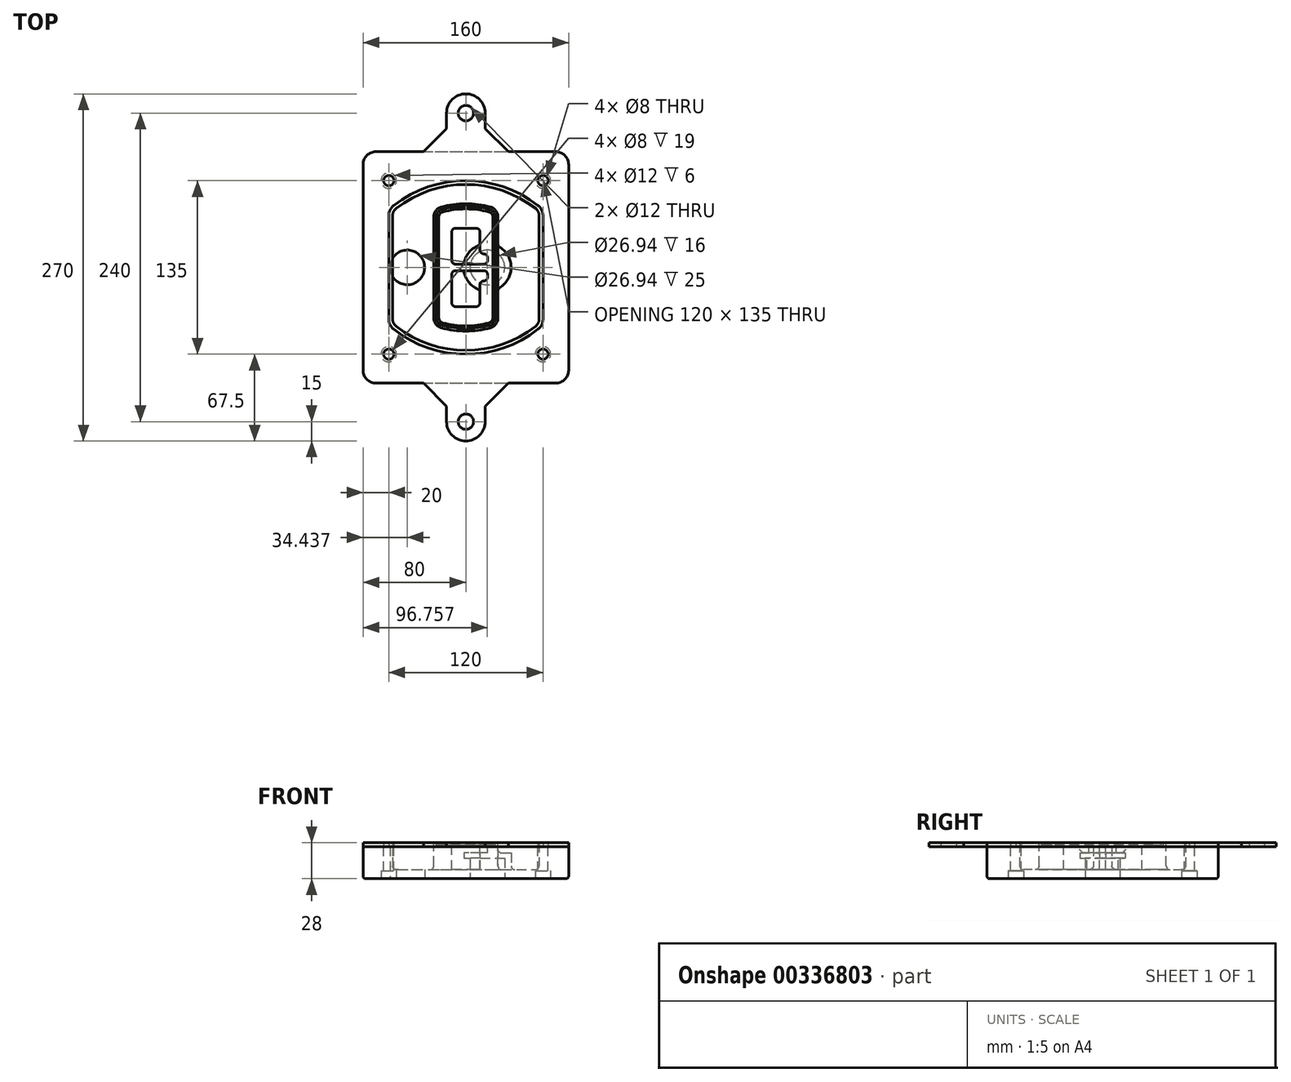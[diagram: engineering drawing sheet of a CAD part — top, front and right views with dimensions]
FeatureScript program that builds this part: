
annotation { "Feature Type Name" : "Feature", "Feature Type Description" : "" }
export const myFeature = defineFeature(function(context is Context, id is Id, definition is map)
    precondition{}
    {
        {
            var Q0;
            Q0=qCreatedBy(makeId("Top.planeOp"),FACE);
            var sketch = newSketch(context, id + "F0", { "sketchPlane" : qUnion([Q0])});
            skPoint(sketch, "E0.rect.middle", {"position": v(0, 0) * mm});
            skLineSegment(sketch, "E1.bottom", {"start": v(-70, -90) * mm, "end": v(70, -90) * mm});
            skLineSegment(sketch, "E1.top", {"start": v(-70, 90) * mm, "end": v(70, 90) * mm});
            skLineSegment(sketch, "E1.left", {"start": v(-80, -80) * mm, "end": v(-80, 80) * mm});
            skLineSegment(sketch, "E1.right", {"start": v(80, -80) * mm, "end": v(80, 80) * mm});
            skLineSegment(sketch, "E2", {"start": v(-80, 90) * mm, "end": v(80, -90) * mm, "construction": true});
            skLineSegment(sketch, "E3", {"start": v(80, 90) * mm, "end": v(-80, -90) * mm, "construction": true});
            skCircle(sketch, "E4", {"center": v(-60, 67.5) * mm, "radius": 4 * mm});
            skCircle(sketch, "E5", {"center": v(60, 67.5) * mm, "radius": 4 * mm});
            skCircle(sketch, "E6", {"center": v(60, -67.5) * mm, "radius": 4 * mm});
            skCircle(sketch, "E7", {"center": v(-60, -67.5) * mm, "radius": 4 * mm});
            skLineSegment(sketch, "E8", {"start": v(-60, 67.5) * mm, "end": v(60, 67.5) * mm, "construction": true});
            skLineSegment(sketch, "E9", {"start": v(60, 67.5) * mm, "end": v(60, -67.5) * mm, "construction": true});
            skLineSegment(sketch, "E10", {"start": v(60, -67.5) * mm, "end": v(-60, -67.5) * mm, "construction": true});
            skLineSegment(sketch, "E11", {"start": v(-60, -67.5) * mm, "end": v(-60, 67.5) * mm, "construction": true});
            skLineSegment(sketch, "E12", {"start": v(-60, 40.3) * mm, "end": v(-60, -40.3) * mm});
            skLineSegment(sketch, "E13", {"start": v(60, 40.3) * mm, "end": v(60, -40.3) * mm});
            skArc(sketch, "E14", {"start": v(56.15, 48.18) * mm, "mid": v(0, 67.5) * mm, "end": v(-56.15, 48.18) * mm});
            skArc(sketch, "E15", {"start": v(-56.15, -48.18) * mm, "mid": v(0, -67.5) * mm, "end": v(56.15, -48.18) * mm});
            skLineSegment(sketch, "E16", {"start": v(-60, 0) * mm, "end": v(60, 0) * mm, "construction": true});
            skPoint(sketch, "E17.visualSharp", {"position": v(-60, -45) * mm});
            skArc(sketch, "E17.filletArc", {"start": v(-60, -40.3) * mm, "mid": v(-58.99, -44.68) * mm, "end": v(-56.15, -48.18) * mm});
            skPoint(sketch, "E18.visualSharp", {"position": v(-60, 45) * mm});
            skArc(sketch, "E18.filletArc", {"start": v(-56.15, 48.18) * mm, "mid": v(-58.99, 44.68) * mm, "end": v(-60, 40.3) * mm});
            skPoint(sketch, "E19.visualSharp", {"position": v(60, 45) * mm});
            skArc(sketch, "E19.filletArc", {"start": v(60, 40.3) * mm, "mid": v(58.99, 44.68) * mm, "end": v(56.15, 48.18) * mm});
            skPoint(sketch, "E20.visualSharp", {"position": v(60, -45) * mm});
            skArc(sketch, "E20.filletArc", {"start": v(56.15, -48.18) * mm, "mid": v(58.99, -44.68) * mm, "end": v(60, -40.3) * mm});
            skPoint(sketch, "E21.visualSharp", {"position": v(-80, 90) * mm});
            skArc(sketch, "E21.filletArc", {"start": v(-70, 90) * mm, "mid": v(-77.07, 87.07) * mm, "end": v(-80, 80) * mm});
            skPoint(sketch, "E22.visualSharp", {"position": v(80, 90) * mm});
            skArc(sketch, "E22.filletArc", {"start": v(80, 80) * mm, "mid": v(77.07, 87.07) * mm, "end": v(70, 90) * mm});
            skPoint(sketch, "E23.visualSharp", {"position": v(80, -90) * mm});
            skArc(sketch, "E23.filletArc", {"start": v(70, -90) * mm, "mid": v(77.07, -87.07) * mm, "end": v(80, -80) * mm});
            skPoint(sketch, "E24.visualSharp", {"position": v(-80, -90) * mm});
            skArc(sketch, "E24.filletArc", {"start": v(-80, -80) * mm, "mid": v(-77.07, -87.07) * mm, "end": v(-70, -90) * mm});
            skArc(sketch, "E25.0", {"start": v(57, 40.3) * mm, "mid": v(56.3, 43.36) * mm, "end": v(54.3, 45.81) * mm});
            skLineSegment(sketch, "E25.1", {"start": v(57, 40.3) * mm, "end": v(57, -40.3) * mm});
            skArc(sketch, "E25.2", {"start": v(54.3, -45.81) * mm, "mid": v(56.3, -43.36) * mm, "end": v(57, -40.3) * mm});
            skArc(sketch, "E25.3", {"start": v(-54.3, -45.81) * mm, "mid": v(0, -64.5) * mm, "end": v(54.3, -45.81) * mm});
            skArc(sketch, "E25.4", {"start": v(-57, -40.3) * mm, "mid": v(-56.3, -43.36) * mm, "end": v(-54.3, -45.81) * mm});
            skArc(sketch, "E25.5", {"start": v(54.3, 45.81) * mm, "mid": v(0, 64.5) * mm, "end": v(-54.3, 45.81) * mm});
            skLineSegment(sketch, "E25.6", {"start": v(-57, 40.3) * mm, "end": v(-57, -40.3) * mm});
            skArc(sketch, "E25.7", {"start": v(-54.3, 45.81) * mm, "mid": v(-56.3, 43.36) * mm, "end": v(-57, 40.3) * mm});
            skArc(sketch, "E26.0", {"start": v(-58.62, 51.33) * mm, "mid": v(-62.58, 46.43) * mm, "end": v(-64, 40.3) * mm});
            skArc(sketch, "E26.1", {"start": v(58.62, 51.33) * mm, "mid": v(0, 71.5) * mm, "end": v(-58.62, 51.33) * mm});
            skArc(sketch, "E26.2", {"start": v(64, 40.3) * mm, "mid": v(62.58, 46.43) * mm, "end": v(58.62, 51.33) * mm});
            skLineSegment(sketch, "E26.3", {"start": v(64, 40.3) * mm, "end": v(64, -40.3) * mm});
            skArc(sketch, "E26.4", {"start": v(58.62, -51.33) * mm, "mid": v(62.58, -46.43) * mm, "end": v(64, -40.3) * mm});
            skLineSegment(sketch, "E26.5", {"start": v(-64, 40.3) * mm, "end": v(-64, -40.3) * mm});
            skArc(sketch, "E26.6", {"start": v(-58.62, -51.33) * mm, "mid": v(0, -71.5) * mm, "end": v(58.62, -51.33) * mm});
            skArc(sketch, "E26.7", {"start": v(-64, -40.3) * mm, "mid": v(-62.58, -46.43) * mm, "end": v(-58.62, -51.33) * mm});
            skSolve(sketch);
        }
        {
            var Q0;
            Q0=makeQuery(id+"F0.imprint","IMPRINT",FACE,{"disambiguationData":[TD([[makeQuery(id+"F0.imprint","IMPRINT",EDGE,{"derivedFrom":sQuery(id+"F0.wireOp",EDGE,"E1.bottom")}),1.0]])]});
            var Q1;
            Q1=makeQuery(id+"F0.imprint","IMPRINT",FACE,{"disambiguationData":[TD([[makeQuery(id+"F0.imprint","IMPRINT",EDGE,{"derivedFrom":sQuery(id+"F0.wireOp",EDGE,"E12")}),1.0]])]});
            var Q2;
            Q2=makeQuery(id+"F0.imprint","IMPRINT",FACE,{"disambiguationData":[TD([[makeQuery(id+"F0.imprint","IMPRINT",EDGE,{"derivedFrom":sQuery(id+"F0.wireOp",EDGE,"E25.0")}),1.0]])]});
            var Q3;
            Q3=makeQuery(id+"F0.imprint","IMPRINT",FACE,{"disambiguationData":[TD([[makeQuery(id+"F0.imprint","IMPRINT",EDGE,{"derivedFrom":sQuery(id+"F0.wireOp",EDGE,"E12")}),-1.0]])]});
            extrude(context, id + "F1", {"entities" : qUnion([Q0, Q1, Q2, Q3]), "oppositeDirection" : true, "depth" : 25 * mm});
        }
        {
            var Q0;
            Q0=makeQuery(id+"F0.imprint","IMPRINT",FACE,{"disambiguationData":[TD([[makeQuery(id+"F0.imprint","IMPRINT",EDGE,{"derivedFrom":sQuery(id+"F0.wireOp",EDGE,"E12")}),1.0]])]});
            extrude(context, id + "F2", {"entities" : qUnion([Q0]), "operationType" : NewBodyOperationType.ADD, "depth" : 3 * mm});
        }
        {
            var Q0;
            Q0=makeQuery(id+"F0.imprint","IMPRINT",FACE,{"disambiguationData":[TD([[makeQuery(id+"F0.imprint","IMPRINT",EDGE,{"derivedFrom":sQuery(id+"F0.wireOp",EDGE,"E25.0")}),1.0]])]});
            extrude(context, id + "F3", {"entities" : qUnion([Q0]), "operationType" : NewBodyOperationType.REMOVE, "oppositeDirection" : true, "depth" : 18 * mm});
        }
        {
            var Q0;
            Q0=makeQuery(id+"F2.opExtrude","CAP_FACE",FACE,{"disambiguationData":[OSD([sQuery(id+"F0.wireOp",EDGE,"E12"),sQuery(id+"F0.wireOp",EDGE,"E13"),sQuery(id+"F0.wireOp",EDGE,"E14"),sQuery(id+"F0.wireOp",EDGE,"E15"),sQuery(id+"F0.wireOp",EDGE,"E17.filletArc"),sQuery(id+"F0.wireOp",EDGE,"E18.filletArc"),sQuery(id+"F0.wireOp",EDGE,"E19.filletArc"),sQuery(id+"F0.wireOp",EDGE,"E20.filletArc"),sQuery(id+"F0.wireOp",EDGE,"E25.0"),sQuery(id+"F0.wireOp",EDGE,"E25.1"),sQuery(id+"F0.wireOp",EDGE,"E25.2"),sQuery(id+"F0.wireOp",EDGE,"E25.3"),sQuery(id+"F0.wireOp",EDGE,"E25.4"),sQuery(id+"F0.wireOp",EDGE,"E25.5"),sQuery(id+"F0.wireOp",EDGE,"E25.6"),sQuery(id+"F0.wireOp",EDGE,"E25.7")])],"isStart":false});
            var sketch = newSketch(context, id + "F4", { "sketchPlane" : qUnion([Q0])});
            skArc(sketch, "E27.0", {"start": v(-19.08, -46.97) * mm, "mid": v(0, -49.5) * mm, "end": v(19.08, -46.97) * mm});
            skArc(sketch, "E28.0", {"start": v(19.08, 46.97) * mm, "mid": v(0, 49.5) * mm, "end": v(-19.08, 46.97) * mm});
            skLineSegment(sketch, "E29", {"start": v(-25, 39.25) * mm, "end": v(-25, -39.25) * mm});
            skLineSegment(sketch, "E30", {"start": v(25, 39.25) * mm, "end": v(25, -39.25) * mm});
            skLineSegment(sketch, "E31", {"start": v(-25, 45.1) * mm, "end": v(25, 45.1) * mm, "construction": true});
            skLineSegment(sketch, "E32", {"start": v(-25, -45.1) * mm, "end": v(25, -45.1) * mm, "construction": true});
            skPoint(sketch, "E33.visualSharp", {"position": v(-25, 45.1) * mm});
            skArc(sketch, "E33.filletArc", {"start": v(-19.08, 46.97) * mm, "mid": v(-23.35, 44.11) * mm, "end": v(-25, 39.25) * mm});
            skPoint(sketch, "E34.visualSharp", {"position": v(25, 45.1) * mm});
            skArc(sketch, "E34.filletArc", {"start": v(25, 39.25) * mm, "mid": v(23.35, 44.11) * mm, "end": v(19.08, 46.97) * mm});
            skPoint(sketch, "E35.visualSharp", {"position": v(25, -45.1) * mm});
            skArc(sketch, "E35.filletArc", {"start": v(19.08, -46.97) * mm, "mid": v(23.35, -44.11) * mm, "end": v(25, -39.25) * mm});
            skPoint(sketch, "E36.visualSharp", {"position": v(-25, -45.1) * mm});
            skArc(sketch, "E36.filletArc", {"start": v(-25, -39.25) * mm, "mid": v(-23.35, -44.11) * mm, "end": v(-19.08, -46.97) * mm});
            skArc(sketch, "E37.0", {"start": v(54.3, 45.81) * mm, "mid": v(0, 64.5) * mm, "end": v(-54.3, 45.81) * mm});
            skArc(sketch, "E37.1", {"start": v(-54.3, 45.81) * mm, "mid": v(-56.3, 43.36) * mm, "end": v(-57, 40.3) * mm});
            skLineSegment(sketch, "E37.2", {"start": v(-57, 40.3) * mm, "end": v(-57, -40.3) * mm});
            skArc(sketch, "E37.3", {"start": v(-57, -40.3) * mm, "mid": v(-56.3, -43.36) * mm, "end": v(-54.3, -45.81) * mm});
            skArc(sketch, "E37.4", {"start": v(-54.3, -45.81) * mm, "mid": v(0, -64.5) * mm, "end": v(54.3, -45.81) * mm});
            skArc(sketch, "E37.5", {"start": v(54.3, -45.81) * mm, "mid": v(56.3, -43.36) * mm, "end": v(57, -40.3) * mm});
            skLineSegment(sketch, "E37.6", {"start": v(57, 40.3) * mm, "end": v(57, -40.3) * mm});
            skArc(sketch, "E37.7", {"start": v(57, 40.3) * mm, "mid": v(56.3, 43.36) * mm, "end": v(54.3, 45.81) * mm});
            skLineSegment(sketch, "E38.0", {"start": v(23, 39.25) * mm, "end": v(23, -39.25) * mm});
            skArc(sketch, "E38.1", {"start": v(18.56, -45.04) * mm, "mid": v(21.76, -42.9) * mm, "end": v(23, -39.25) * mm});
            skArc(sketch, "E38.2", {"start": v(-18.56, -45.04) * mm, "mid": v(0, -47.5) * mm, "end": v(18.56, -45.04) * mm});
            skArc(sketch, "E38.3", {"start": v(-23, -39.25) * mm, "mid": v(-21.76, -42.9) * mm, "end": v(-18.56, -45.04) * mm});
            skLineSegment(sketch, "E38.4", {"start": v(-23, 39.25) * mm, "end": v(-23, -39.25) * mm});
            skArc(sketch, "E38.5", {"start": v(23, 39.25) * mm, "mid": v(21.76, 42.9) * mm, "end": v(18.56, 45.04) * mm});
            skArc(sketch, "E38.6", {"start": v(-18.56, 45.04) * mm, "mid": v(-21.76, 42.9) * mm, "end": v(-23, 39.25) * mm});
            skArc(sketch, "E38.7", {"start": v(18.56, 45.04) * mm, "mid": v(0, 47.5) * mm, "end": v(-18.56, 45.04) * mm});
            skArc(sketch, "E39.0", {"start": v(21, 39.25) * mm, "mid": v(20.18, 41.68) * mm, "end": v(18.04, 43.1) * mm});
            skLineSegment(sketch, "E39.1", {"start": v(21, 39.25) * mm, "end": v(21, -39.25) * mm});
            skArc(sketch, "E39.2", {"start": v(18.04, -43.1) * mm, "mid": v(20.18, -41.68) * mm, "end": v(21, -39.25) * mm});
            skArc(sketch, "E39.3", {"start": v(-18.04, -43.1) * mm, "mid": v(0, -45.5) * mm, "end": v(18.04, -43.1) * mm});
            skArc(sketch, "E39.4", {"start": v(-21, -39.25) * mm, "mid": v(-20.18, -41.68) * mm, "end": v(-18.04, -43.1) * mm});
            skArc(sketch, "E39.5", {"start": v(18.04, 43.1) * mm, "mid": v(0, 45.5) * mm, "end": v(-18.04, 43.1) * mm});
            skLineSegment(sketch, "E39.6", {"start": v(-21, 39.25) * mm, "end": v(-21, -39.25) * mm});
            skArc(sketch, "E39.7", {"start": v(-18.04, 43.1) * mm, "mid": v(-20.18, 41.68) * mm, "end": v(-21, 39.25) * mm});
            skLineSegment(sketch, "E40", {"start": v(-25, 0) * mm, "end": v(25, 0) * mm, "construction": true});
            skLineSegment(sketch, "E41", {"start": v(-11, 5.5) * mm, "end": v(-11, 27.5) * mm});
            skLineSegment(sketch, "E42", {"start": v(-8, 30.5) * mm, "end": v(8, 30.5) * mm});
            skLineSegment(sketch, "E43", {"start": v(11, 27.5) * mm, "end": v(11, 13.5) * mm});
            skLineSegment(sketch, "E44", {"start": v(14, 10.5) * mm, "end": v(14, 10.5) * mm});
            skLineSegment(sketch, "E45", {"start": v(17, 7.5) * mm, "end": v(17, 5.5) * mm});
            skLineSegment(sketch, "E46", {"start": v(14, 2.5) * mm, "end": v(-8, 2.5) * mm});
            skPoint(sketch, "E47.visualSharp", {"position": v(-11, 30.5) * mm});
            skArc(sketch, "E47.filletArc", {"start": v(-8, 30.5) * mm, "mid": v(-10.12, 29.62) * mm, "end": v(-11, 27.5) * mm});
            skPoint(sketch, "E48.visualSharp", {"position": v(11, 30.5) * mm});
            skArc(sketch, "E48.filletArc", {"start": v(11, 27.5) * mm, "mid": v(10.12, 29.62) * mm, "end": v(8, 30.5) * mm});
            skPoint(sketch, "E49.visualSharp", {"position": v(11, 10.5) * mm});
            skArc(sketch, "E49.filletArc", {"start": v(11, 13.5) * mm, "mid": v(11.88, 11.38) * mm, "end": v(14, 10.5) * mm});
            skPoint(sketch, "E50.visualSharp", {"position": v(17, 10.5) * mm});
            skArc(sketch, "E50.filletArc", {"start": v(17, 7.5) * mm, "mid": v(16.12, 9.62) * mm, "end": v(14, 10.5) * mm});
            skPoint(sketch, "E51.visualSharp", {"position": v(17, 2.5) * mm});
            skArc(sketch, "E51.filletArc", {"start": v(14, 2.5) * mm, "mid": v(16.12, 3.38) * mm, "end": v(17, 5.5) * mm});
            skPoint(sketch, "E52.visualSharp", {"position": v(-11, 2.5) * mm});
            skArc(sketch, "E52.filletArc", {"start": v(-11, 5.5) * mm, "mid": v(-10.12, 3.38) * mm, "end": v(-8, 2.5) * mm});
            skLineSegment(sketch, "E53.0.MirrorCS", {"start": v(14, -2.5) * mm, "end": v(-8, -2.5) * mm});
            skArc(sketch, "E54.0.MirrorCS", {"start": v(-11, -5.5) * mm, "mid": v(-10.12, -3.38) * mm, "end": v(-8, -2.5) * mm});
            skLineSegment(sketch, "E55.0.MirrorCS", {"start": v(-11, -5.5) * mm, "end": v(-11, -27.5) * mm});
            skArc(sketch, "E56.0.MirrorCS", {"start": v(-8, -30.5) * mm, "mid": v(-10.12, -29.62) * mm, "end": v(-11, -27.5) * mm});
            skLineSegment(sketch, "E57.0.MirrorCS", {"start": v(-8, -30.5) * mm, "end": v(8, -30.5) * mm});
            skArc(sketch, "E58.0.MirrorCS", {"start": v(11, -27.5) * mm, "mid": v(10.12, -29.62) * mm, "end": v(8, -30.5) * mm});
            skLineSegment(sketch, "E59.0.MirrorCS", {"start": v(11, -27.5) * mm, "end": v(11, -13.5) * mm});
            skArc(sketch, "E60.0.MirrorCS", {"start": v(11, -13.5) * mm, "mid": v(11.88, -11.38) * mm, "end": v(14, -10.5) * mm});
            skArc(sketch, "E61.0.MirrorCS", {"start": v(17, -7.5) * mm, "mid": v(16.12, -9.62) * mm, "end": v(14, -10.5) * mm});
            skLineSegment(sketch, "E62.0.MirrorCS", {"start": v(17, -7.5) * mm, "end": v(17, -5.5) * mm});
            skArc(sketch, "E63.0.MirrorCS", {"start": v(14, -2.5) * mm, "mid": v(16.12, -3.38) * mm, "end": v(17, -5.5) * mm});
            skSolve(sketch);
        }
        {
            var Q0;
            Q0=makeQuery(id+"F4.imprint","IMPRINT",FACE,{"disambiguationData":[TD([[makeQuery(id+"F4.imprint","IMPRINT",EDGE,{"derivedFrom":sQuery(id+"F4.wireOp",EDGE,"E27.0")}),1.0]])]});
            var Q1;
            Q1=makeQuery(id+"F4.imprint","IMPRINT",FACE,{"disambiguationData":[TD([[makeQuery(id+"F4.imprint","IMPRINT",EDGE,{"derivedFrom":sQuery(id+"F4.wireOp",EDGE,"E38.0")}),-1.0]])]});
            var Q2;
            Q2=makeQuery(id+"F4.imprint","IMPRINT",FACE,{"disambiguationData":[TD([[makeQuery(id+"F4.imprint","IMPRINT",EDGE,{"derivedFrom":sQuery(id+"F4.wireOp",EDGE,"E39.0")}),1.0]])]});
            extrude(context, id + "F5", {"entities" : qUnion([Q0, Q1, Q2]), "operationType" : NewBodyOperationType.ADD, "endBound" : BoundingType.UP_TO_NEXT, "oppositeDirection" : true, "depth" : 25 * mm});
        }
        {
            var Q0;
            Q0=makeQuery(id+"F4.imprint","IMPRINT",FACE,{"disambiguationData":[TD([[makeQuery(id+"F4.imprint","IMPRINT",EDGE,{"derivedFrom":sQuery(id+"F4.wireOp",EDGE,"E38.0")}),-1.0]])]});
            extrude(context, id + "F6", {"entities" : qUnion([Q0]), "operationType" : NewBodyOperationType.REMOVE, "oppositeDirection" : true, "depth" : 2 * mm});
        }
        {
            var Q0;
            Q0=makeQuery(id+"F1.opExtrude","CAP_FACE",FACE,{"disambiguationData":[OSD([sQuery(id+"F0.wireOp",EDGE,"E1.bottom"),sQuery(id+"F0.wireOp",EDGE,"E1.top"),sQuery(id+"F0.wireOp",EDGE,"E1.left"),sQuery(id+"F0.wireOp",EDGE,"E1.right"),sQuery(id+"F0.wireOp",EDGE,"E4"),sQuery(id+"F0.wireOp",EDGE,"E5"),sQuery(id+"F0.wireOp",EDGE,"E6"),sQuery(id+"F0.wireOp",EDGE,"E7"),sQuery(id+"F0.wireOp",EDGE,"E21.filletArc"),sQuery(id+"F0.wireOp",EDGE,"E22.filletArc"),sQuery(id+"F0.wireOp",EDGE,"E23.filletArc"),sQuery(id+"F0.wireOp",EDGE,"E24.filletArc")])],"isStart":false});
            var sketch = newSketch(context, id + "F7", { "sketchPlane" : qUnion([Q0])});
            skCircle(sketch, "E64", {"center": v(16.76, 0) * mm, "radius": 13.47 * mm});
            skCircle(sketch, "E65", {"center": v(-45.56, 0) * mm, "radius": 13.47 * mm});
            skLineSegment(sketch, "E66", {"start": v(80, 0) * mm, "end": v(-80, 0) * mm});
            skCircle(sketch, "E67", {"center": v(16.76, 0) * mm, "radius": 18.47 * mm});
            skCircle(sketch, "E68", {"center": v(60, -67.5) * mm, "radius": 6 * mm});
            skCircle(sketch, "E69", {"center": v(-60, -67.5) * mm, "radius": 6 * mm});
            skCircle(sketch, "E70", {"center": v(-60, 67.5) * mm, "radius": 6 * mm});
            skCircle(sketch, "E71", {"center": v(60, 67.5) * mm, "radius": 6 * mm});
            skSolve(sketch);
        }
        {
            var Q0;
            {var subQ1=sQuery(id+"F7.wireOp",EDGE,"E66");var subQ4=sQuery(id+"F7.wireOp",EDGE,"E64");var subQ6=makeQuery(id+"F7.imprint","INTERSECT",VERTEX,{"disambiguationData":[OD(0.0)],"derivedFrom":[subQ4,subQ1]});Q0=makeQuery(id+"F7.imprint","IMPRINT",FACE,{"disambiguationData":[TD([[makeQuery(id+"F7.imprint","IMPRINT",EDGE,{"disambiguationData":[TD([[subQ6,-1.0]])],"derivedFrom":subQ4}),-1.0]])]});}
            var Q1;
            {var subQ0=sQuery(id+"F7.wireOp",EDGE,"E66");var subQ1=sQuery(id+"F7.wireOp",EDGE,"E64");var subQ3=makeQuery(id+"F7.imprint","INTERSECT",VERTEX,{"disambiguationData":[OD(0.0)],"derivedFrom":[subQ1,subQ0]});Q1=makeQuery(id+"F7.imprint","IMPRINT",FACE,{"disambiguationData":[TD([[makeQuery(id+"F7.imprint","IMPRINT",EDGE,{"disambiguationData":[TD([[subQ3,-1.0]])],"derivedFrom":subQ1}),1.0]])]});}
            var Q2;
            {var subQ0=sQuery(id+"F7.wireOp",EDGE,"E66");var subQ1=sQuery(id+"F7.wireOp",EDGE,"E64");var subQ3=makeQuery(id+"F7.imprint","INTERSECT",VERTEX,{"disambiguationData":[OD(0.0)],"derivedFrom":[subQ1,subQ0]});Q2=makeQuery(id+"F7.imprint","IMPRINT",FACE,{"disambiguationData":[TD([[makeQuery(id+"F7.imprint","IMPRINT",EDGE,{"disambiguationData":[TD([[subQ3,1.0]])],"derivedFrom":subQ1}),1.0]])]});}
            var Q3;
            {var subQ1=sQuery(id+"F7.wireOp",EDGE,"E66");var subQ4=sQuery(id+"F7.wireOp",EDGE,"E64");var subQ6=makeQuery(id+"F7.imprint","INTERSECT",VERTEX,{"disambiguationData":[OD(0.0)],"derivedFrom":[subQ4,subQ1]});Q3=makeQuery(id+"F7.imprint","IMPRINT",FACE,{"disambiguationData":[TD([[makeQuery(id+"F7.imprint","IMPRINT",EDGE,{"disambiguationData":[TD([[subQ6,1.0]])],"derivedFrom":subQ4}),-1.0]])]});}
            extrude(context, id + "F8", {"entities" : qUnion([Q0, Q1, Q2, Q3]), "operationType" : NewBodyOperationType.ADD, "oppositeDirection" : true, "depth" : 20 * mm});
        }
        {
            var Q0;
            {var subQ0=sQuery(id+"F7.wireOp",EDGE,"E66");var subQ1=sQuery(id+"F7.wireOp",EDGE,"E64");var subQ3=makeQuery(id+"F7.imprint","INTERSECT",VERTEX,{"disambiguationData":[OD(0.0)],"derivedFrom":[subQ1,subQ0]});Q0=makeQuery(id+"F7.imprint","IMPRINT",FACE,{"disambiguationData":[TD([[makeQuery(id+"F7.imprint","IMPRINT",EDGE,{"disambiguationData":[TD([[subQ3,-1.0]])],"derivedFrom":subQ1}),1.0]])]});}
            var Q1;
            {var subQ0=sQuery(id+"F7.wireOp",EDGE,"E66");var subQ1=sQuery(id+"F7.wireOp",EDGE,"E64");var subQ3=makeQuery(id+"F7.imprint","INTERSECT",VERTEX,{"disambiguationData":[OD(0.0)],"derivedFrom":[subQ1,subQ0]});Q1=makeQuery(id+"F7.imprint","IMPRINT",FACE,{"disambiguationData":[TD([[makeQuery(id+"F7.imprint","IMPRINT",EDGE,{"disambiguationData":[TD([[subQ3,1.0]])],"derivedFrom":subQ1}),1.0]])]});}
            extrude(context, id + "F9", {"entities" : qUnion([Q0, Q1]), "operationType" : NewBodyOperationType.REMOVE, "oppositeDirection" : true, "depth" : 16 * mm});
        }
        {
            var Q0;
            {var subQ0=sQuery(id+"F7.wireOp",EDGE,"E66");var subQ1=sQuery(id+"F7.wireOp",EDGE,"E65");var subQ3=makeQuery(id+"F7.imprint","INTERSECT",VERTEX,{"disambiguationData":[OD(0.0)],"derivedFrom":[subQ1,subQ0]});Q0=makeQuery(id+"F7.imprint","IMPRINT",FACE,{"disambiguationData":[TD([[makeQuery(id+"F7.imprint","IMPRINT",EDGE,{"disambiguationData":[TD([[subQ3,-1.0]])],"derivedFrom":subQ1}),1.0]])]});}
            var Q1;
            {var subQ0=sQuery(id+"F7.wireOp",EDGE,"E66");var subQ1=sQuery(id+"F7.wireOp",EDGE,"E65");var subQ3=makeQuery(id+"F7.imprint","INTERSECT",VERTEX,{"disambiguationData":[OD(0.0)],"derivedFrom":[subQ1,subQ0]});Q1=makeQuery(id+"F7.imprint","IMPRINT",FACE,{"disambiguationData":[TD([[makeQuery(id+"F7.imprint","IMPRINT",EDGE,{"disambiguationData":[TD([[subQ3,1.0]])],"derivedFrom":subQ1}),1.0]])]});}
            extrude(context, id + "F10", {"entities" : qUnion([Q0, Q1]), "operationType" : NewBodyOperationType.REMOVE, "oppositeDirection" : true, "depth" : 25 * mm});
        }
        {
            var Q0;
            Q0=makeQuery(id+"F7.imprint","IMPRINT",FACE,{"disambiguationData":[TD([[makeQuery(id+"F7.imprint","IMPRINT",EDGE,{"derivedFrom":sQuery(id+"F7.wireOp",EDGE,"E68")}),1.0]])]});
            var Q1;
            Q1=makeQuery(id+"F7.imprint","IMPRINT",FACE,{"disambiguationData":[TD([[makeQuery(id+"F7.imprint","IMPRINT",EDGE,{"derivedFrom":makeQuery(id+"F1.opExtrude","CAP_EDGE",EDGE,{"disambiguationData":[OSD([sQuery(id+"F0.wireOp",EDGE,"E5")])],"isStart":false})}),-1.0]])]});
            var Q2;
            Q2=makeQuery(id+"F7.imprint","IMPRINT",FACE,{"disambiguationData":[TD([[makeQuery(id+"F7.imprint","IMPRINT",EDGE,{"derivedFrom":sQuery(id+"F7.wireOp",EDGE,"E69")}),1.0]])]});
            var Q3;
            Q3=makeQuery(id+"F7.imprint","IMPRINT",FACE,{"disambiguationData":[TD([[makeQuery(id+"F7.imprint","IMPRINT",EDGE,{"derivedFrom":makeQuery(id+"F1.opExtrude","CAP_EDGE",EDGE,{"disambiguationData":[OSD([sQuery(id+"F0.wireOp",EDGE,"E4")])],"isStart":false})}),-1.0]])]});
            var Q4;
            Q4=makeQuery(id+"F7.imprint","IMPRINT",FACE,{"disambiguationData":[TD([[makeQuery(id+"F7.imprint","IMPRINT",EDGE,{"derivedFrom":sQuery(id+"F7.wireOp",EDGE,"E70")}),1.0]])]});
            var Q5;
            Q5=makeQuery(id+"F7.imprint","IMPRINT",FACE,{"disambiguationData":[TD([[makeQuery(id+"F7.imprint","IMPRINT",EDGE,{"derivedFrom":makeQuery(id+"F1.opExtrude","CAP_EDGE",EDGE,{"disambiguationData":[OSD([sQuery(id+"F0.wireOp",EDGE,"E7")])],"isStart":false})}),-1.0]])]});
            var Q6;
            Q6=makeQuery(id+"F7.imprint","IMPRINT",FACE,{"disambiguationData":[TD([[makeQuery(id+"F7.imprint","IMPRINT",EDGE,{"derivedFrom":sQuery(id+"F7.wireOp",EDGE,"E71")}),1.0]])]});
            var Q7;
            Q7=makeQuery(id+"F7.imprint","IMPRINT",FACE,{"disambiguationData":[TD([[makeQuery(id+"F7.imprint","IMPRINT",EDGE,{"derivedFrom":makeQuery(id+"F1.opExtrude","CAP_EDGE",EDGE,{"disambiguationData":[OSD([sQuery(id+"F0.wireOp",EDGE,"E6")])],"isStart":false})}),-1.0]])]});
            extrude(context, id + "F11", {"entities" : qUnion([Q0, Q1, Q2, Q3, Q4, Q5, Q6, Q7]), "operationType" : NewBodyOperationType.REMOVE, "oppositeDirection" : true, "depth" : 6 * mm});
        }
        {
            var Q0;
            Q0=makeQuery(id+"F9.boolean.opBoolean","COPY",FACE,{"derivedFrom":makeQuery(id+"F9.opExtrude","CAP_FACE",FACE,{"disambiguationData":[OSD([sQuery(id+"F7.wireOp",EDGE,"E64")])],"isStart":false})});
            var sketch = newSketch(context, id + "F12", { "sketchPlane" : qUnion([Q0])});
            skArc(sketch, "E72.0", {"start": v(11, 17.55) * mm, "mid": v(2.57, 11.82) * mm, "end": v(-1.54, 2.5) * mm});
            skArc(sketch, "E72.1", {"start": v(-1.54, -2.5) * mm, "mid": v(2.57, -11.82) * mm, "end": v(11, -17.55) * mm});
            skLineSegment(sketch, "E73", {"start": v(-1.54, -2.5) * mm, "end": v(14, -2.5) * mm});
            skLineSegment(sketch, "E74.0", {"start": v(14, 2.5) * mm, "end": v(-1.54, 2.5) * mm});
            skArc(sketch, "E74.1", {"start": v(14, 2.5) * mm, "mid": v(16.12, 3.38) * mm, "end": v(17, 5.5) * mm});
            skLineSegment(sketch, "E74.2", {"start": v(17, 7.5) * mm, "end": v(17, 5.5) * mm});
            skArc(sketch, "E74.3", {"start": v(17, 7.5) * mm, "mid": v(16.12, 9.62) * mm, "end": v(14, 10.5) * mm});
            skArc(sketch, "E74.4", {"start": v(11, 13.5) * mm, "mid": v(11.88, 11.38) * mm, "end": v(14, 10.5) * mm});
            skLineSegment(sketch, "E74.5", {"start": v(11, 17.55) * mm, "end": v(11, 13.5) * mm});
            skLineSegment(sketch, "E74.7", {"start": v(14, -2.5) * mm, "end": v(-1.54, -2.5) * mm});
            skArc(sketch, "E74.8", {"start": v(14, -2.5) * mm, "mid": v(16.12, -3.38) * mm, "end": v(17, -5.5) * mm});
            skLineSegment(sketch, "E74.9", {"start": v(17, -7.5) * mm, "end": v(17, -5.5) * mm});
            skArc(sketch, "E74.10", {"start": v(17, -7.5) * mm, "mid": v(16.12, -9.62) * mm, "end": v(14, -10.5) * mm});
            skArc(sketch, "E74.11", {"start": v(11, -13.5) * mm, "mid": v(11.88, -11.38) * mm, "end": v(14, -10.5) * mm});
            skLineSegment(sketch, "E74.12", {"start": v(11, -17.55) * mm, "end": v(11, -13.5) * mm});
            skPoint(sketch, "E75.orphan", {"position": v(11, -27.5) * mm});
            skPoint(sketch, "E76.orphan", {"position": v(-8, -2.5) * mm});
            skPoint(sketch, "E77.orphan", {"position": v(-8, 2.5) * mm});
            skPoint(sketch, "E78.orphan", {"position": v(11, 27.5) * mm});
            skSolve(sketch);
        }
        {
            var Q0;
            {var subQ7=sQuery(id+"F12.wireOp",EDGE,"E72.0");var subQ14=sQuery(id+"F12.wireOp",EDGE,"E72.1");var subQ16=sQuery(id+"F12.wireOp",EDGE,"E74.1");var subQ18=sQuery(id+"F12.wireOp",EDGE,"E74.8");Q0=qUnion([makeQuery(id+"F12.imprint","IMPRINT",FACE,{"disambiguationData":[TD([[makeQuery(id+"F12.imprint","IMPRINT",EDGE,{"derivedFrom":subQ7}),1.0]])]}),makeQuery(id+"F12.imprint","IMPRINT",FACE,{"disambiguationData":[TD([[makeQuery(id+"F12.imprint","IMPRINT",EDGE,{"derivedFrom":subQ14}),1.0]])]}),makeQuery(id+"F12.imprint","IMPRINT",FACE,{"disambiguationData":[TD([[makeQuery(id+"F12.imprint","IMPRINT",EDGE,{"derivedFrom":subQ16}),1.0]])]}),makeQuery(id+"F12.imprint","IMPRINT",FACE,{"disambiguationData":[TD([[makeQuery(id+"F12.imprint","IMPRINT",EDGE,{"derivedFrom":subQ18}),-1.0]])]})]);}
            var Q1;
            Q1=makeQuery(id+"F5.boolean.opBoolean","SPLIT",FACE,{"disambiguationData":[TD([makeQuery(id+"F5.opExtrude","SWEPT_FACE",FACE,{"disambiguationData":[OSD([sQuery(id+"F4.wireOp",EDGE,"E41")])]})])],"derivedFrom":makeQuery(id+"F3.boolean.opBoolean","COPY",FACE,{"derivedFrom":makeQuery(id+"F3.opExtrude","CAP_FACE",FACE,{"disambiguationData":[OSD([sQuery(id+"F0.wireOp",EDGE,"E25.0"),sQuery(id+"F0.wireOp",EDGE,"E25.1"),sQuery(id+"F0.wireOp",EDGE,"E25.2"),sQuery(id+"F0.wireOp",EDGE,"E25.3"),sQuery(id+"F0.wireOp",EDGE,"E25.4"),sQuery(id+"F0.wireOp",EDGE,"E25.5"),sQuery(id+"F0.wireOp",EDGE,"E25.6"),sQuery(id+"F0.wireOp",EDGE,"E25.7")])],"isStart":false})})});
            extrude(context, id + "F13", {"entities" : qUnion([Q0]), "operationType" : NewBodyOperationType.REMOVE, "endBound" : BoundingType.UP_TO_SURFACE, "endBoundEntityFace" : qUnion([Q1]), "depth" : 25 * mm});
        }
        {
            var Q0;
            Q0=makeQuery(id+"F3.boolean.opBoolean","COPY",EDGE,{"derivedFrom":makeQuery(id+"F3.opExtrude","CAP_EDGE",EDGE,{"disambiguationData":[OSD([sQuery(id+"F0.wireOp",EDGE,"E25.6")])],"isStart":false})});
            var Q1;
            Q1=makeQuery(id+"F8.boolean.opBoolean","INTERSECT",EDGE,{"derivedFrom":[makeQuery(id+"F5.opExtrude","SWEPT_FACE",FACE,{"disambiguationData":[OSD([sQuery(id+"F4.wireOp",EDGE,"E30")])]}),makeQuery(id+"F8.opExtrude","CAP_FACE",FACE,{"disambiguationData":[OSD([sQuery(id+"F7.wireOp",EDGE,"E67")])],"isStart":false})]});
            var Q2;
            Q2=makeQuery(id+"F8.boolean.opBoolean","INTERSECT",EDGE,{"disambiguationData":[OD(1.0)],"derivedFrom":[makeQuery(id+"F5.opExtrude","SWEPT_FACE",FACE,{"disambiguationData":[OSD([sQuery(id+"F4.wireOp",EDGE,"E30")])]}),makeQuery(id+"F8.opExtrude","SWEPT_FACE",FACE,{"disambiguationData":[OSD([sQuery(id+"F7.wireOp",EDGE,"E67")])]})]});
            var Q3;
            {var subQ0=sQuery(id+"F4.wireOp",EDGE,"E30");Q3=makeQuery(id+"F8.boolean.opBoolean","SPLIT",EDGE,{"disambiguationData":[TD([makeQuery(id+"F5.opExtrude","SWEPT_FACE",FACE,{"disambiguationData":[OSD([sQuery(id+"F4.wireOp",EDGE,"E35.filletArc")])]})])],"derivedFrom":makeQuery(id+"F5.opExtrude","CAP_EDGE",EDGE,{"disambiguationData":[OSD([subQ0])],"isStart":false})});}
            var Q4;
            {var subQ0=sQuery(id+"F0.wireOp",EDGE,"E25.7");var subQ1=sQuery(id+"F0.wireOp",EDGE,"E25.1");var subQ2=sQuery(id+"F0.wireOp",EDGE,"E25.6");var subQ3=sQuery(id+"F0.wireOp",EDGE,"E25.5");var subQ4=sQuery(id+"F0.wireOp",EDGE,"E25.4");var subQ5=sQuery(id+"F0.wireOp",EDGE,"E25.0");var subQ6=sQuery(id+"F0.wireOp",EDGE,"E25.2");var subQ7=sQuery(id+"F0.wireOp",EDGE,"E25.3");Q4=makeQuery(id+"F8.boolean.opBoolean","INTERSECT",EDGE,{"derivedFrom":[makeQuery(id+"F5.boolean.opBoolean","SPLIT",FACE,{"disambiguationData":[TD([makeQuery(id+"F2.opExtrude","SWEPT_FACE",FACE,{"disambiguationData":[OSD([subQ5])]})])],"derivedFrom":makeQuery(id+"F3.boolean.opBoolean","COPY",FACE,{"derivedFrom":makeQuery(id+"F3.opExtrude","CAP_FACE",FACE,{"disambiguationData":[OSD([subQ5,subQ1,subQ6,subQ7,subQ4,subQ3,subQ2,subQ0])],"isStart":false})})}),makeQuery(id+"F8.opExtrude","SWEPT_FACE",FACE,{"disambiguationData":[OSD([sQuery(id+"F7.wireOp",EDGE,"E67")])]})]});}
            var Q5;
            Q5=makeQuery(id+"F8.boolean.opBoolean","INTERSECT",EDGE,{"disambiguationData":[OD(0.0)],"derivedFrom":[makeQuery(id+"F5.opExtrude","SWEPT_FACE",FACE,{"disambiguationData":[OSD([sQuery(id+"F4.wireOp",EDGE,"E30")])]}),makeQuery(id+"F8.opExtrude","SWEPT_FACE",FACE,{"disambiguationData":[OSD([sQuery(id+"F7.wireOp",EDGE,"E67")])]})]});
            fillet(context, id + "F14", {"entities" : qUnion([Q0, Q1, Q2, Q3, Q4, Q5]), "radius" : 3 * mm, "tangentPropagation" : true, "allowEdgeOverflow" : false});
        }
        {
            var Q0;
            Q0=makeQuery(id+"F1.opExtrude","CAP_EDGE",EDGE,{"disambiguationData":[OSD([sQuery(id+"F0.wireOp",EDGE,"E1.bottom")])],"isStart":false});
            fillet(context, id + "F15", {"entities" : qUnion([Q0]), "radius" : 2 * mm, "tangentPropagation" : true, "allowEdgeOverflow" : false});
        }
        {
            var Q0;
            {var subQ0=sQuery(id+"F0.wireOp",EDGE,"E21.filletArc");var subQ1=sQuery(id+"F0.wireOp",EDGE,"E7");var subQ2=sQuery(id+"F0.wireOp",EDGE,"E6");var subQ3=sQuery(id+"F0.wireOp",EDGE,"E5");var subQ4=sQuery(id+"F0.wireOp",EDGE,"E4");var subQ5=sQuery(id+"F0.wireOp",EDGE,"E22.filletArc");var subQ6=sQuery(id+"F0.wireOp",EDGE,"E1.bottom");var subQ7=sQuery(id+"F0.wireOp",EDGE,"E1.right");var subQ8=sQuery(id+"F0.wireOp",EDGE,"E1.top");var subQ9=sQuery(id+"F0.wireOp",EDGE,"E1.left");var subQ10=sQuery(id+"F0.wireOp",EDGE,"E23.filletArc");var subQ11=sQuery(id+"F0.wireOp",EDGE,"E24.filletArc");Q0=makeQuery(id+"F2.boolean.opBoolean","SPLIT",FACE,{"disambiguationData":[TD([makeQuery(id+"F1.opExtrude","SWEPT_FACE",FACE,{"disambiguationData":[OSD([subQ6])]})])],"derivedFrom":makeQuery(id+"F1.opExtrude","CAP_FACE",FACE,{"disambiguationData":[OSD([subQ6,subQ8,subQ9,subQ7,subQ4,subQ3,subQ2,subQ1,subQ0,subQ5,subQ10,subQ11])],"isStart":true})});}
            var sketch = newSketch(context, id + "F16", { "sketchPlane" : qUnion([Q0])});
            skLineSegment(sketch, "E79.0", {"start": v(-70, 90) * mm, "end": v(70, 90) * mm});
            skArc(sketch, "E79.1", {"start": v(-70, 90) * mm, "mid": v(-77.07, 87.07) * mm, "end": v(-80, 80) * mm});
            skLineSegment(sketch, "E79.2", {"start": v(-80, -80) * mm, "end": v(-80, 80) * mm});
            skCircle(sketch, "E79.3", {"center": v(-60, 67.5) * mm, "radius": 4 * mm});
            skArc(sketch, "E79.4", {"start": v(-56.15, 48.18) * mm, "mid": v(-58.99, 44.68) * mm, "end": v(-60, 40.3) * mm});
            skArc(sketch, "E79.5", {"start": v(56.15, 48.18) * mm, "mid": v(0, 67.5) * mm, "end": v(-56.15, 48.18) * mm});
            skLineSegment(sketch, "E79.6", {"start": v(-60, 40.3) * mm, "end": v(-60, -40.3) * mm});
            skArc(sketch, "E79.7", {"start": v(60, 40.3) * mm, "mid": v(58.99, 44.68) * mm, "end": v(56.15, 48.18) * mm});
            skLineSegment(sketch, "E79.8", {"start": v(60, 40.3) * mm, "end": v(60, -40.3) * mm});
            skLineSegment(sketch, "E79.9", {"start": v(80, -80) * mm, "end": v(80, 80) * mm});
            skArc(sketch, "E79.10", {"start": v(80, 80) * mm, "mid": v(77.07, 87.07) * mm, "end": v(70, 90) * mm});
            skCircle(sketch, "E79.11", {"center": v(60, 67.5) * mm, "radius": 4 * mm});
            skCircle(sketch, "E79.12", {"center": v(60, -67.5) * mm, "radius": 4 * mm});
            skArc(sketch, "E79.13", {"start": v(70, -90) * mm, "mid": v(77.07, -87.07) * mm, "end": v(80, -80) * mm});
            skArc(sketch, "E79.14", {"start": v(56.15, -48.18) * mm, "mid": v(58.99, -44.68) * mm, "end": v(60, -40.3) * mm});
            skArc(sketch, "E79.15", {"start": v(-56.15, -48.18) * mm, "mid": v(0, -67.5) * mm, "end": v(56.15, -48.18) * mm});
            skArc(sketch, "E79.16", {"start": v(-60, -40.3) * mm, "mid": v(-58.99, -44.68) * mm, "end": v(-56.15, -48.18) * mm});
            skCircle(sketch, "E79.17", {"center": v(-60, -67.5) * mm, "radius": 4 * mm});
            skArc(sketch, "E79.18", {"start": v(-80, -80) * mm, "mid": v(-77.07, -87.07) * mm, "end": v(-70, -90) * mm});
            skLineSegment(sketch, "E79.19", {"start": v(-70, -90) * mm, "end": v(70, -90) * mm});
            skLineSegment(sketch, "E80", {"start": v(0, 90) * mm, "end": v(0, 120) * mm, "construction": true});
            skCircle(sketch, "E81", {"center": v(0, 120) * mm, "radius": 6 * mm});
            skArc(sketch, "E82", {"start": v(15, 120) * mm, "mid": v(0, 135) * mm, "end": v(-15, 120) * mm});
            skLineSegment(sketch, "E83", {"start": v(15, 120) * mm, "end": v(15, 108) * mm});
            skLineSegment(sketch, "E84", {"start": v(-15, 120) * mm, "end": v(-15, 108) * mm});
            skLineSegment(sketch, "E85", {"start": v(-15, 108) * mm, "end": v(-33, 90) * mm});
            skLineSegment(sketch, "E86", {"start": v(15, 108) * mm, "end": v(33, 90) * mm});
            skArc(sketch, "E87.MirrorCS", {"start": v(-15, 120) * mm, "mid": v(0, 135) * mm, "end": v(15, 120) * mm});
            skLineSegment(sketch, "E88.MirrorCS", {"start": v(70, 90) * mm, "end": v(-70, 90) * mm});
            skLineSegment(sketch, "E89", {"start": v(80, 0) * mm, "end": v(-80, 0) * mm, "construction": true});
            skLineSegment(sketch, "E90.MirrorCS", {"start": v(-15, -108) * mm, "end": v(-33, -90) * mm});
            skLineSegment(sketch, "E91.MirrorCS", {"start": v(-15, -120) * mm, "end": v(-15, -108) * mm});
            skArc(sketch, "E92.MirrorCS", {"start": v(15, -120) * mm, "mid": v(0, -135) * mm, "end": v(-15, -120) * mm});
            skLineSegment(sketch, "E93.MirrorCS", {"start": v(15, -120) * mm, "end": v(15, -108) * mm});
            skLineSegment(sketch, "E94.MirrorCS", {"start": v(15, -108) * mm, "end": v(33, -90) * mm});
            skCircle(sketch, "E95.MirrorC", {"center": v(0, -120) * mm, "radius": 6 * mm});
            skLineSegment(sketch, "E96.MirrorCS", {"start": v(0, -90) * mm, "end": v(0, -120) * mm, "construction": true});
            skSolve(sketch);
        }
        {
            var Q0;
            Q0 = qSketchRegion(id + "F16", true);
            var Q1;
            Q1=makeQuery(id+"F2.opExtrude","CAP_FACE",FACE,{"disambiguationData":[OSD([sQuery(id+"F0.wireOp",EDGE,"E12"),sQuery(id+"F0.wireOp",EDGE,"E13"),sQuery(id+"F0.wireOp",EDGE,"E14"),sQuery(id+"F0.wireOp",EDGE,"E15"),sQuery(id+"F0.wireOp",EDGE,"E17.filletArc"),sQuery(id+"F0.wireOp",EDGE,"E18.filletArc"),sQuery(id+"F0.wireOp",EDGE,"E19.filletArc"),sQuery(id+"F0.wireOp",EDGE,"E20.filletArc"),sQuery(id+"F0.wireOp",EDGE,"E25.0"),sQuery(id+"F0.wireOp",EDGE,"E25.1"),sQuery(id+"F0.wireOp",EDGE,"E25.2"),sQuery(id+"F0.wireOp",EDGE,"E25.3"),sQuery(id+"F0.wireOp",EDGE,"E25.4"),sQuery(id+"F0.wireOp",EDGE,"E25.5"),sQuery(id+"F0.wireOp",EDGE,"E25.6"),sQuery(id+"F0.wireOp",EDGE,"E25.7")])],"isStart":false});
            extrude(context, id + "F17", {"entities" : qUnion([Q0]), "endBound" : BoundingType.UP_TO_SURFACE, "endBoundEntityFace" : qUnion([Q1]), "depth" : 25 * mm});
        }
    });
